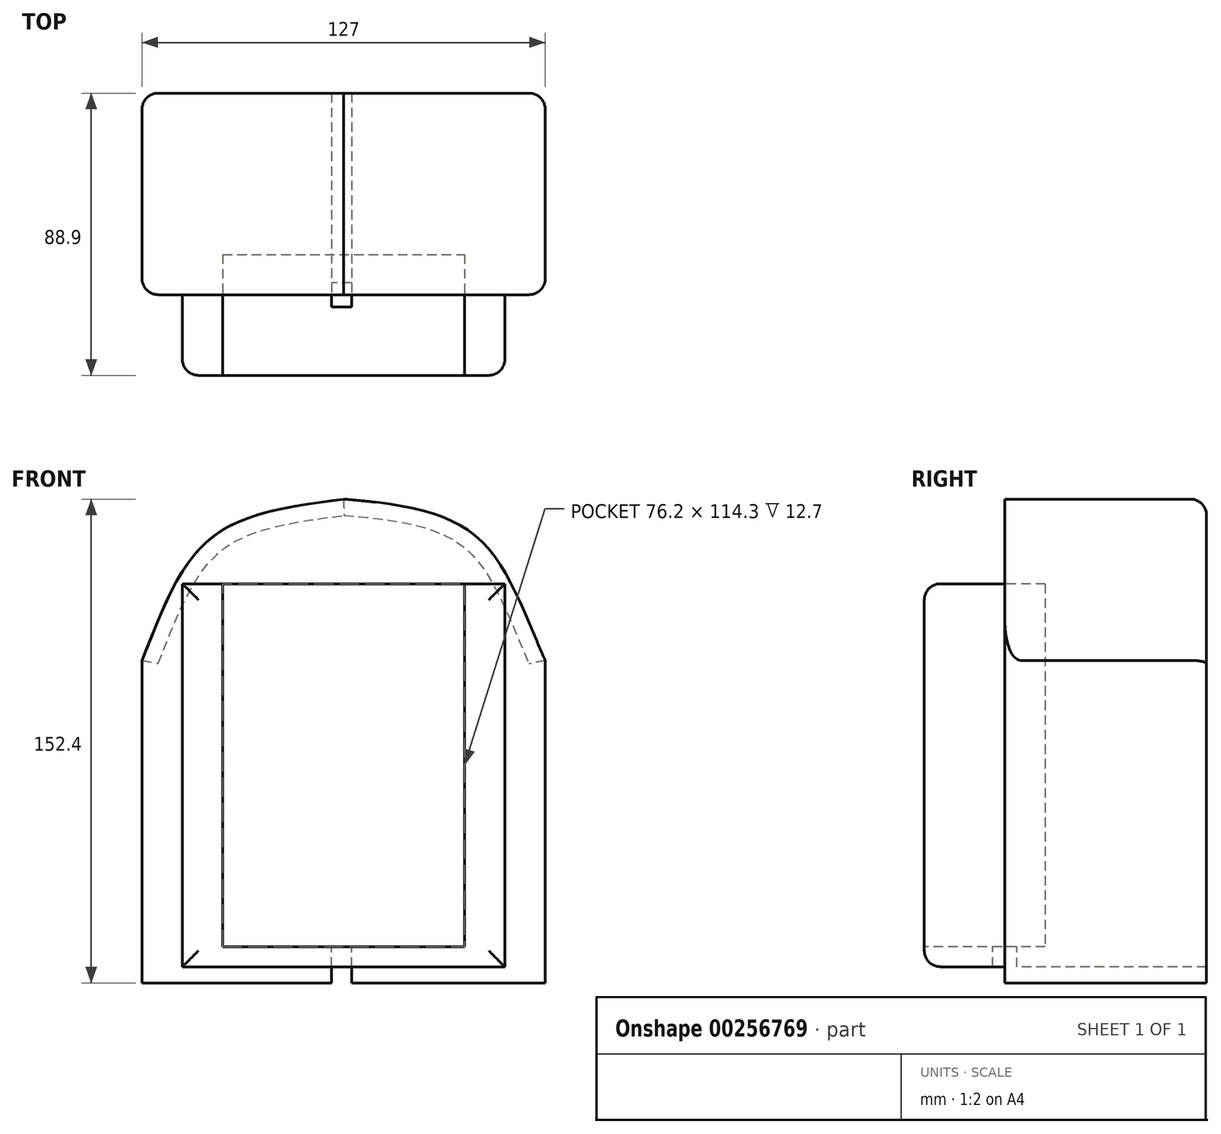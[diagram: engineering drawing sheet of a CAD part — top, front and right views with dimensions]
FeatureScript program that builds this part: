
annotation { "Feature Type Name" : "Feature", "Feature Type Description" : "" }
export const myFeature = defineFeature(function(context is Context, id is Id, definition is map)
    precondition{}
    {
        {
            var Q0;
            Q0=qCreatedBy(makeId("Front.planeOp"),FACE);
            var sketch = newSketch(context, id + "F0", { "sketchPlane" : qUnion([Q0])});
            skLineSegment(sketch, "E0.bottom", {"start": v(-60.67, 75.9) * mm, "end": v(66.33, 75.9) * mm});
            skLineSegment(sketch, "E0.top", {"start": v(-60.67, -76.5) * mm, "end": v(66.33, -76.5) * mm});
            skLineSegment(sketch, "E0.left", {"start": v(-60.67, 75.9) * mm, "end": v(-60.67, -76.5) * mm});
            skLineSegment(sketch, "E0.right", {"start": v(66.33, 75.9) * mm, "end": v(66.33, -76.5) * mm});
            skSolve(sketch);
        }
        {
            var Q0;
            Q0 = qSketchRegion(id + "F0", true);
            extrude(context, id + "F1", {"entities" : qUnion([Q0]), "depth" : 63.5 * mm});
        }
        {
            var Q0;
            Q0=makeQuery(id+"F1.opExtrude","CAP_FACE",FACE,{"disambiguationData":[OSD([sQuery(id+"F0.wireOp",EDGE,"E0.bottom"),sQuery(id+"F0.wireOp",EDGE,"E0.top"),sQuery(id+"F0.wireOp",EDGE,"E0.left"),sQuery(id+"F0.wireOp",EDGE,"E0.right")])],"isStart":false});
            var sketch = newSketch(context, id + "F2", { "sketchPlane" : qUnion([Q0])});
            skFitSpline(sketch, "E1", {"points": [v(2.83, 75.9) * mm, v(-39.08, 63.5) * mm, v(-60.67, 25.1) * mm], "startDerivative": vector(-92.15, -12.54) * mm, "endDerivative": vector(-34.77, -85.15) * mm});
            skFitSpline(sketch, "E2", {"points": [v(2.83, 75.9) * mm, v(44.74, 64.03) * mm, v(66.33, 25.1) * mm], "startDerivative": vector(102.88, -8.59) * mm, "endDerivative": vector(39.75, -88.81) * mm});
            skSolve(sketch);
        }
        {
            var Q0;
            Q0 = qSketchRegion(id + "F2", true);
            var Q1;
            {var subQ0=sQuery(id+"F2.wireOp",EDGE,"E1");Q1=makeQuery(id+"F2.imprint","IMPRINT",FACE,{"disambiguationData":[TD([[makeQuery(id+"F2.imprint","IMPRINT",EDGE,{"derivedFrom":subQ0}),-1.0]])]});}
            var Q2;
            {var subQ0=sQuery(id+"F2.wireOp",EDGE,"E2");Q2=makeQuery(id+"F2.imprint","IMPRINT",FACE,{"disambiguationData":[TD([[makeQuery(id+"F2.imprint","IMPRINT",EDGE,{"derivedFrom":subQ0}),1.0]])]});}
            extrude(context, id + "F3", {"entities" : qUnion([Q0, Q1, Q2]), "operationType" : NewBodyOperationType.REMOVE, "endBound" : BoundingType.THROUGH_ALL, "oppositeDirection" : true, "depth" : 25.4 * mm});
        }
        {
            var Q0;
            Q0=makeQuery(id+"F1.opExtrude","CAP_FACE",FACE,{"disambiguationData":[OSD([sQuery(id+"F0.wireOp",EDGE,"E0.bottom"),sQuery(id+"F0.wireOp",EDGE,"E0.top"),sQuery(id+"F0.wireOp",EDGE,"E0.left"),sQuery(id+"F0.wireOp",EDGE,"E0.right")])],"isStart":false});
            var sketch = newSketch(context, id + "F4", { "sketchPlane" : qUnion([Q0])});
            skLineSegment(sketch, "E3.bottom", {"start": v(-47.97, -71.42) * mm, "end": v(53.63, -71.42) * mm});
            skLineSegment(sketch, "E3.top", {"start": v(-47.97, 49.23) * mm, "end": v(53.63, 49.23) * mm});
            skLineSegment(sketch, "E3.left", {"start": v(-47.97, -71.42) * mm, "end": v(-47.97, 49.23) * mm});
            skLineSegment(sketch, "E3.right", {"start": v(53.63, -71.42) * mm, "end": v(53.63, 49.23) * mm});
            skSolve(sketch);
        }
        {
            var Q0;
            Q0 = qSketchRegion(id + "F4", true);
            extrude(context, id + "F5", {"entities" : qUnion([Q0]), "operationType" : NewBodyOperationType.ADD, "depth" : 25.4 * mm});
        }
        {
            var Q0;
            Q0=makeQuery(id+"F5.opExtrude","CAP_FACE",FACE,{"disambiguationData":[OSD([sQuery(id+"F4.wireOp",EDGE,"E3.bottom"),sQuery(id+"F4.wireOp",EDGE,"E3.top"),sQuery(id+"F4.wireOp",EDGE,"E3.left"),sQuery(id+"F4.wireOp",EDGE,"E3.right")])],"isStart":false});
            var sketch = newSketch(context, id + "F6", { "sketchPlane" : qUnion([Q0])});
            skLineSegment(sketch, "E4.bottom", {"start": v(-35.27, 49.23) * mm, "end": v(40.93, 49.23) * mm});
            skLineSegment(sketch, "E4.top", {"start": v(-35.27, -65.07) * mm, "end": v(40.93, -65.07) * mm});
            skLineSegment(sketch, "E4.left", {"start": v(-35.27, 49.23) * mm, "end": v(-35.27, -65.07) * mm});
            skLineSegment(sketch, "E4.right", {"start": v(40.93, 49.23) * mm, "end": v(40.93, -65.07) * mm});
            skSolve(sketch);
        }
        {
            var Q0;
            Q0 = qSketchRegion(id + "F6", true);
            extrude(context, id + "F7", {"entities" : qUnion([Q0]), "operationType" : NewBodyOperationType.REMOVE, "oppositeDirection" : true, "depth" : 38.1 * mm});
        }
        {
            var Q0;
            Q0=makeQuery(id+"F3.boolean.opBoolean","COPY",EDGE,{"derivedFrom":makeQuery(id+"F3.opExtrude","SWEPT_EDGE",EDGE,{"disambiguationData":[OSD([sQuery(id+"F0.wireOp",EDGE,"E0.left"),sQuery(id+"F2.wireOp",EDGE,"E1")])]})});
            var Q1;
            Q1=makeQuery(id+"F1.opExtrude","CAP_EDGE",EDGE,{"disambiguationData":[OSD([sQuery(id+"F0.wireOp",EDGE,"E0.left")])],"isStart":false});
            var Q2;
            Q2=makeQuery(id+"F3.boolean.opBoolean","COPY",EDGE,{"derivedFrom":makeQuery(id+"F3.opExtrude","CAP_EDGE",EDGE,{"disambiguationData":[OSD([sQuery(id+"F2.wireOp",EDGE,"E1")])],"isStart":true})});
            var Q3;
            Q3=makeQuery(id+"F7.boolean.opBoolean","SPLIT",EDGE,{"disambiguationData":[topologyDisambiguationEdgeConnected([makeQuery(id+"F1.opExtrude","CAP_FACE",FACE,{"disambiguationData":[OSD([sQuery(id+"F0.wireOp",EDGE,"E0.bottom"),sQuery(id+"F0.wireOp",EDGE,"E0.top"),sQuery(id+"F0.wireOp",EDGE,"E0.left"),sQuery(id+"F0.wireOp",EDGE,"E0.right")])],"isStart":false}),makeQuery(id+"F7.opExtrude","SWEPT_FACE",FACE,{"disambiguationData":[OSD([sQuery(id+"F6.wireOp",EDGE,"E4.bottom")])]})])],"derivedFrom":makeQuery(id+"F5.opExtrude","CAP_EDGE",EDGE,{"disambiguationData":[OSD([sQuery(id+"F4.wireOp",EDGE,"E3.top")])],"isStart":true})});
            var Q4;
            Q4=makeQuery(id+"F3.boolean.opBoolean","COPY",EDGE,{"derivedFrom":makeQuery(id+"F3.opExtrude","CAP_EDGE",EDGE,{"disambiguationData":[OSD([sQuery(id+"F2.wireOp",EDGE,"E2")])],"isStart":true})});
            var Q5;
            Q5=makeQuery(id+"F1.opExtrude","CAP_EDGE",EDGE,{"disambiguationData":[OSD([sQuery(id+"F0.wireOp",EDGE,"E0.right")])],"isStart":false});
            var Q6;
            Q6=makeQuery(id+"F7.boolean.opBoolean","COPY",EDGE,{"derivedFrom":makeQuery(id+"F7.opExtrude","CAP_EDGE",EDGE,{"disambiguationData":[OSD([sQuery(id+"F6.wireOp",EDGE,"E4.left")])],"isStart":true})});
            var Q7;
            Q7=makeQuery(id+"F7.boolean.opBoolean","COPY",EDGE,{"derivedFrom":makeQuery(id+"F7.opExtrude","CAP_EDGE",EDGE,{"disambiguationData":[OSD([sQuery(id+"F6.wireOp",EDGE,"E4.right")])],"isStart":true})});
            var Q8;
            Q8=makeQuery(id+"F5.opExtrude","CAP_EDGE",EDGE,{"disambiguationData":[OSD([sQuery(id+"F4.wireOp",EDGE,"E3.bottom")])],"isStart":false});
            var Q9;
            Q9=makeQuery(id+"F5.opExtrude","CAP_EDGE",EDGE,{"disambiguationData":[OSD([sQuery(id+"F4.wireOp",EDGE,"E3.left")])],"isStart":false});
            var Q10;
            Q10=makeQuery(id+"F5.opExtrude","CAP_EDGE",EDGE,{"disambiguationData":[OSD([sQuery(id+"F4.wireOp",EDGE,"E3.right")])],"isStart":false});
            var Q11;
            {var subQ0=sQuery(id+"F4.wireOp",EDGE,"E3.left");var subQ1=sQuery(id+"F4.wireOp",EDGE,"E3.top");Q11=makeQuery(id+"F7.boolean.opBoolean","SPLIT",EDGE,{"disambiguationData":[TD([makeQuery(id+"F5.opExtrude","SWEPT_FACE",FACE,{"disambiguationData":[OSD([subQ0])]})])],"derivedFrom":makeQuery(id+"F5.opExtrude","CAP_EDGE",EDGE,{"disambiguationData":[OSD([subQ1])],"isStart":false})});}
            var Q12;
            {var subQ0=sQuery(id+"F4.wireOp",EDGE,"E3.right");var subQ1=sQuery(id+"F4.wireOp",EDGE,"E3.top");Q12=makeQuery(id+"F7.boolean.opBoolean","SPLIT",EDGE,{"disambiguationData":[TD([makeQuery(id+"F5.opExtrude","SWEPT_FACE",FACE,{"disambiguationData":[OSD([subQ0])]})])],"derivedFrom":makeQuery(id+"F5.opExtrude","CAP_EDGE",EDGE,{"disambiguationData":[OSD([subQ1])],"isStart":false})});}
            var Q13;
            Q13=makeQuery(id+"F1.opExtrude","CAP_EDGE",EDGE,{"disambiguationData":[OSD([sQuery(id+"F0.wireOp",EDGE,"E0.left")])],"isStart":true});
            var Q14;
            Q14=makeQuery(id+"F3.boolean.opBoolean","INTERSECT",EDGE,{"derivedFrom":[makeQuery(id+"F1.opExtrude","CAP_FACE",FACE,{"disambiguationData":[OSD([sQuery(id+"F0.wireOp",EDGE,"E0.bottom"),sQuery(id+"F0.wireOp",EDGE,"E0.top"),sQuery(id+"F0.wireOp",EDGE,"E0.left"),sQuery(id+"F0.wireOp",EDGE,"E0.right")])],"isStart":true}),makeQuery(id+"F3.opExtrude","SWEPT_FACE",FACE,{"disambiguationData":[OSD([sQuery(id+"F2.wireOp",EDGE,"E1")])]})]});
            var Q15;
            Q15=makeQuery(id+"F3.boolean.opBoolean","INTERSECT",EDGE,{"derivedFrom":[makeQuery(id+"F1.opExtrude","CAP_FACE",FACE,{"disambiguationData":[OSD([sQuery(id+"F0.wireOp",EDGE,"E0.bottom"),sQuery(id+"F0.wireOp",EDGE,"E0.top"),sQuery(id+"F0.wireOp",EDGE,"E0.left"),sQuery(id+"F0.wireOp",EDGE,"E0.right")])],"isStart":true}),makeQuery(id+"F3.opExtrude","SWEPT_FACE",FACE,{"disambiguationData":[OSD([sQuery(id+"F2.wireOp",EDGE,"E2")])]})]});
            var Q16;
            Q16=makeQuery(id+"F1.opExtrude","CAP_EDGE",EDGE,{"disambiguationData":[OSD([sQuery(id+"F0.wireOp",EDGE,"E0.right")])],"isStart":true});
            var Q17;
            Q17=makeQuery(id+"F3.boolean.opBoolean","COPY",EDGE,{"derivedFrom":makeQuery(id+"F3.opExtrude","SWEPT_EDGE",EDGE,{"disambiguationData":[OSD([sQuery(id+"F0.wireOp",EDGE,"E0.right"),sQuery(id+"F2.wireOp",EDGE,"E2")])]})});
            fillet(context, id + "F8", {"entities" : qUnion([Q0, Q1, Q2, Q3, Q4, Q5, Q6, Q7, Q8, Q9, Q10, Q11, Q12, Q13, Q14, Q15, Q16, Q17]), "radius" : 5.08 * mm, "tangentPropagation" : true, "allowEdgeOverflow" : false});
        }
        {
            var Q0;
            Q0=makeQuery(id+"F7.boolean.opBoolean","COPY",FACE,{"derivedFrom":makeQuery(id+"F7.opExtrude","SWEPT_FACE",FACE,{"disambiguationData":[OSD([sQuery(id+"F6.wireOp",EDGE,"E4.top")])]})});
            var sketch = newSketch(context, id + "F9", { "sketchPlane" : qUnion([Q0])});
            skLineSegment(sketch, "E5.bottom", {"start": v(5.37, -59.7) * mm, "end": v(-0.98, -59.7) * mm});
            skLineSegment(sketch, "E5.top", {"start": v(5.37, -67.31) * mm, "end": v(-0.98, -67.31) * mm});
            skLineSegment(sketch, "E5.left", {"start": v(5.37, -59.7) * mm, "end": v(5.37, -67.31) * mm});
            skLineSegment(sketch, "E5.right", {"start": v(-0.98, -59.7) * mm, "end": v(-0.98, -67.31) * mm});
            skSolve(sketch);
        }
        {
            var Q0;
            Q0 = qSketchRegion(id + "F9", true);
            extrude(context, id + "F10", {"entities" : qUnion([Q0]), "operationType" : NewBodyOperationType.REMOVE, "endBound" : BoundingType.THROUGH_ALL, "oppositeDirection" : true, "depth" : 25.4 * mm});
        }
        {
            var Q0;
            Q0=makeQuery(id+"F10.boolean.opBoolean","COPY",FACE,{"derivedFrom":makeQuery(id+"F10.opExtrude","SWEPT_FACE",FACE,{"disambiguationData":[OSD([sQuery(id+"F9.wireOp",EDGE,"E5.bottom")])]})});
            var sketch = newSketch(context, id + "F11", { "sketchPlane" : qUnion([Q0])});
            skLineSegment(sketch, "E6.bottom", {"start": v(-0.98, -71.5) * mm, "end": v(5.37, -71.5) * mm});
            skLineSegment(sketch, "E6.top", {"start": v(-0.98, -76.5) * mm, "end": v(5.37, -76.5) * mm});
            skLineSegment(sketch, "E6.left", {"start": v(-0.98, -71.5) * mm, "end": v(-0.98, -76.5) * mm});
            skLineSegment(sketch, "E6.right", {"start": v(5.37, -71.5) * mm, "end": v(5.37, -76.5) * mm});
            skSolve(sketch);
        }
        {
            var Q0;
            Q0 = qSketchRegion(id + "F11", true);
            extrude(context, id + "F12", {"entities" : qUnion([Q0]), "operationType" : NewBodyOperationType.REMOVE, "endBound" : BoundingType.THROUGH_ALL, "oppositeDirection" : true, "depth" : 25.4 * mm});
        }
    });
